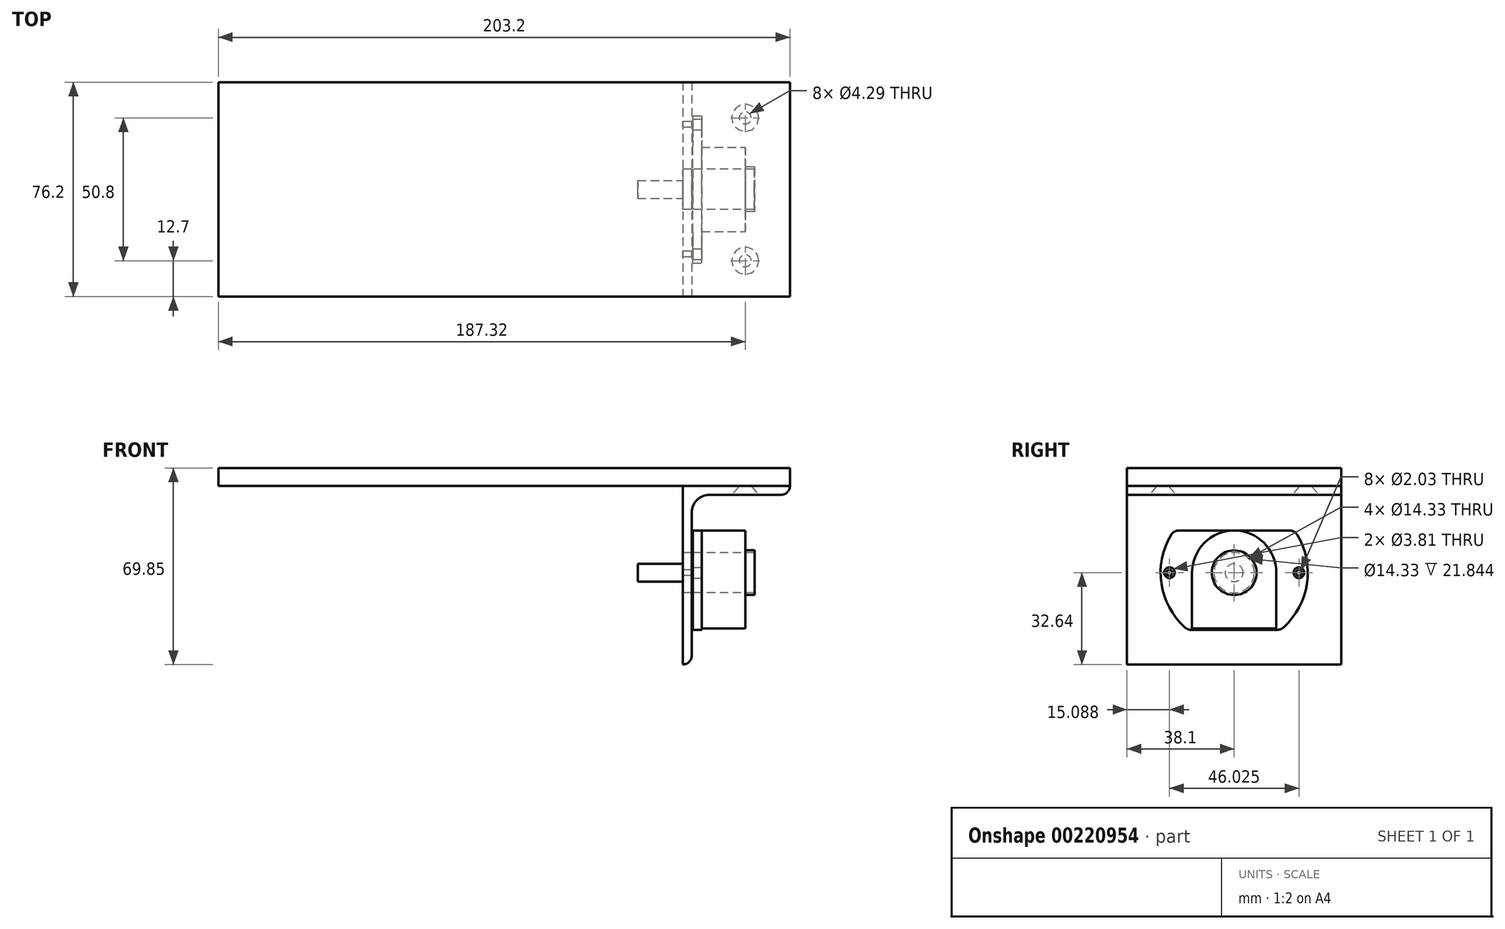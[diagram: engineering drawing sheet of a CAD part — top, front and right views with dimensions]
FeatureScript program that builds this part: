
annotation { "Feature Type Name" : "Feature", "Feature Type Description" : "" }
export const myFeature = defineFeature(function(context is Context, id is Id, definition is map)
    precondition{}
    {
        {
            var Q0;
            Q0=qCreatedBy(makeId("Right.planeOp"),FACE);
            var sketch = newSketch(context, id + "F0", { "sketchPlane" : qUnion([Q0])});
            skCircle(sketch, "E0", {"center": v(0, 0) * mm, "radius": 7.94 * mm});
            skCircle(sketch, "E1", {"center": v(0, 0) * mm, "radius": 14.99 * mm});
            skLineSegment(sketch, "E2", {"start": v(-14.99, 0) * mm, "end": v(-14.99, -19.81) * mm});
            skLineSegment(sketch, "E3", {"start": v(-14.99, -19.81) * mm, "end": v(14.99, -19.81) * mm});
            skLineSegment(sketch, "E4", {"start": v(14.99, -19.81) * mm, "end": v(14.99, 0) * mm});
            skSolve(sketch);
        }
        {
            var Q0;
            Q0=makeQuery(id+"F0.imprint","IMPRINT",FACE,{"disambiguationData":[TD([[makeQuery(id+"F0.imprint","IMPRINT",EDGE,{"derivedFrom":sQuery(id+"F0.wireOp",EDGE,"E0")}),1.0]])]});
            extrude(context, id + "F1", {"entities" : qUnion([Q0]), "depth" : 3.3 * mm});
        }
        {
            var Q0;
            Q0=makeQuery(id+"F0.imprint","IMPRINT",FACE,{"disambiguationData":[TD([[makeQuery(id+"F0.imprint","IMPRINT",EDGE,{"derivedFrom":sQuery(id+"F0.wireOp",EDGE,"E0")}),-1.0]])]});
            var Q1;
            {var subQ0=sQuery(id+"F0.wireOp",EDGE,"E2");Q1=makeQuery(id+"F0.imprint","IMPRINT",FACE,{"disambiguationData":[TD([[makeQuery(id+"F0.imprint","IMPRINT",EDGE,{"derivedFrom":subQ0}),1.0]])]});}
            var Q2;
            Q2=makeQuery(id+"F0.imprint","IMPRINT",FACE,{"disambiguationData":[TD([[makeQuery(id+"F0.imprint","IMPRINT",EDGE,{"derivedFrom":sQuery(id+"F0.wireOp",EDGE,"E0")}),1.0]])]});
            extrude(context, id + "F2", {"entities" : qUnion([Q0, Q1, Q2]), "operationType" : NewBodyOperationType.ADD, "oppositeDirection" : true, "depth" : 15.5 * mm});
        }
        {
            var Q0;
            Q0=makeQuery(id+"F2.opExtrude","CAP_FACE",FACE,{"disambiguationData":[OSD([sQuery(id+"F0.wireOp",EDGE,"E1"),sQuery(id+"F0.wireOp",EDGE,"E2"),sQuery(id+"F0.wireOp",EDGE,"E3"),sQuery(id+"F0.wireOp",EDGE,"E4")])],"isStart":false});
            var sketch = newSketch(context, id + "F3", { "sketchPlane" : qUnion([Q0])});
            skArc(sketch, "E5", {"start": v(-21.44, 14.99) * mm, "mid": v(-25.9, -3.64) * mm, "end": v(-16.48, -20.32) * mm});
            skLineSegment(sketch, "E6", {"start": v(21.44, 14.99) * mm, "end": v(-21.44, 14.99) * mm});
            skLineSegment(sketch, "E7", {"start": v(16.48, -20.32) * mm, "end": v(-16.48, -20.32) * mm});
            skArc(sketch, "E8.trimOffspring", {"start": v(16.48, -20.32) * mm, "mid": v(25.9, -3.64) * mm, "end": v(21.44, 14.99) * mm});
            skCircle(sketch, "E9", {"center": v(23.01, 0) * mm, "radius": 1.9 * mm});
            skCircle(sketch, "E10", {"center": v(-23.01, 0) * mm, "radius": 1.9 * mm});
            skLineSegment(sketch, "E11", {"start": v(23.01, 0) * mm, "end": v(-23.01, 0) * mm, "construction": true});
            skCircle(sketch, "E12", {"center": v(0, 0) * mm, "radius": 3.18 * mm});
            skSolve(sketch);
        }
        {
            var Q0;
            Q0=makeQuery(id+"F3.imprint","IMPRINT",FACE,{"disambiguationData":[TD([[makeQuery(id+"F3.imprint","IMPRINT",EDGE,{"derivedFrom":sQuery(id+"F3.wireOp",EDGE,"E12")}),-1.0]])]});
            var Q1;
            {var subQ2=sQuery(id+"F3.wireOp",EDGE,"E5");Q1=makeQuery(id+"F3.imprint","IMPRINT",FACE,{"disambiguationData":[TD([[makeQuery(id+"F3.imprint","IMPRINT",EDGE,{"derivedFrom":subQ2}),1.0]])]});}
            var Q2;
            Q2=makeQuery(id+"F3.imprint","IMPRINT",FACE,{"disambiguationData":[TD([[makeQuery(id+"F3.imprint","IMPRINT",EDGE,{"derivedFrom":sQuery(id+"F3.wireOp",EDGE,"E12")}),1.0]])]});
            extrude(context, id + "F4", {"entities" : qUnion([Q0, Q1, Q2]), "operationType" : NewBodyOperationType.ADD, "depth" : 3.17 * mm});
        }
        {
            var Q0;
            Q0=makeQuery(id+"F4.opExtrude","CAP_FACE",FACE,{"disambiguationData":[OSD([sQuery(id+"F3.wireOp",EDGE,"E5"),sQuery(id+"F3.wireOp",EDGE,"E6"),sQuery(id+"F3.wireOp",EDGE,"E7"),sQuery(id+"F3.wireOp",EDGE,"E8.trimOffspring"),sQuery(id+"F3.wireOp",EDGE,"E9"),sQuery(id+"F3.wireOp",EDGE,"E10")])],"isStart":false});
            var sketch = newSketch(context, id + "F5", { "sketchPlane" : qUnion([Q0])});
            skCircle(sketch, "E13", {"center": v(0, 0) * mm, "radius": 3.18 * mm});
            skCircle(sketch, "E14", {"center": v(0, 0) * mm, "radius": 6.35 * mm});
            skSolve(sketch);
        }
        {
            var Q0;
            Q0=makeQuery(id+"F5.imprint","IMPRINT",FACE,{"disambiguationData":[TD([[makeQuery(id+"F5.imprint","IMPRINT",EDGE,{"derivedFrom":sQuery(id+"F5.wireOp",EDGE,"E13")}),1.0]])]});
            extrude(context, id + "F6", {"entities" : qUnion([Q0]), "operationType" : NewBodyOperationType.ADD, "depth" : 19.56 * mm});
        }
        {
            var Q0;
            Q0=makeQuery(id+"F5.imprint","IMPRINT",FACE,{"disambiguationData":[TD([[makeQuery(id+"F5.imprint","IMPRINT",EDGE,{"derivedFrom":sQuery(id+"F5.wireOp",EDGE,"E13")}),-1.0]])]});
            extrude(context, id + "F7", {"entities" : qUnion([Q0]), "operationType" : NewBodyOperationType.ADD, "depth" : 0.5 * mm});
        }
        {
            var Q0;
            Q0=makeQuery(id+"F4.opExtrude","SWEPT_EDGE",EDGE,{"disambiguationData":[OSD([sQuery(id+"F3.wireOp",EDGE,"E6"),sQuery(id+"F3.wireOp",EDGE,"E8.trimOffspring")])]});
            var Q1;
            Q1=makeQuery(id+"F4.opExtrude","SWEPT_EDGE",EDGE,{"disambiguationData":[OSD([sQuery(id+"F3.wireOp",EDGE,"E5"),sQuery(id+"F3.wireOp",EDGE,"E6")])]});
            var Q2;
            Q2=makeQuery(id+"F4.opExtrude","SWEPT_EDGE",EDGE,{"disambiguationData":[OSD([sQuery(id+"F3.wireOp",EDGE,"E5"),sQuery(id+"F3.wireOp",EDGE,"E7")])]});
            var Q3;
            Q3=makeQuery(id+"F4.opExtrude","SWEPT_EDGE",EDGE,{"disambiguationData":[OSD([sQuery(id+"F3.wireOp",EDGE,"E7"),sQuery(id+"F3.wireOp",EDGE,"E8.trimOffspring")])]});
            fillet(context, id + "F8", {"entities" : qUnion([Q0, Q1, Q2, Q3]), "radius" : 3.17 * mm, "tangentPropagation" : true, "allowEdgeOverflow" : false});
        }
        {
            var Q0;
            Q0=qCreatedBy(makeId("Front.planeOp"),FACE);
            cPlane(context, id + "F9", {"entities" : qUnion([Q0]), "cplaneType" : CPlaneType.OFFSET, "offset" : 38.1 * mm, "width" : 152.4 * mm, "height" : 152.4 * mm});
        }
        {
            var Q0;
            Q0=qCreatedBy(id+"F9.planeOp",FACE);
            var sketch = newSketch(context, id + "F10", { "sketchPlane" : qUnion([Q0])});
            skLineSegment(sketch, "E15", {"start": v(-22.22, -32.64) * mm, "end": v(-22.23, 30.86) * mm});
            skLineSegment(sketch, "E16", {"start": v(-22.23, 30.86) * mm, "end": v(15.87, 30.86) * mm});
            skLineSegment(sketch, "E17", {"start": v(15.87, 30.86) * mm, "end": v(15.87, 27.69) * mm});
            skLineSegment(sketch, "E18", {"start": v(15.87, 27.69) * mm, "end": v(-19.05, 27.69) * mm});
            skLineSegment(sketch, "E19", {"start": v(-19.05, 27.69) * mm, "end": v(-19.05, -32.64) * mm});
            skLineSegment(sketch, "E20", {"start": v(-19.05, -32.64) * mm, "end": v(-22.22, -32.64) * mm});
            skSolve(sketch);
        }
        {
            var Q0;
            Q0 = qSketchRegion(id + "F10", true);
            extrude(context, id + "F11", {"entities" : qUnion([Q0]), "oppositeDirection" : true, "depth" : 76.2 * mm});
        }
        {
            var Q0;
            Q0=makeQuery(id+"F11.opExtrude","SWEPT_EDGE",EDGE,{"disambiguationData":[OSD([sQuery(id+"F10.wireOp",EDGE,"E17"),sQuery(id+"F10.wireOp",EDGE,"E18")])]});
            var Q1;
            Q1=makeQuery(id+"F11.opExtrude","SWEPT_EDGE",EDGE,{"disambiguationData":[OSD([sQuery(id+"F10.wireOp",EDGE,"E19"),sQuery(id+"F10.wireOp",EDGE,"E20")])]});
            fillet(context, id + "F12", {"entities" : qUnion([Q0, Q1]), "radius" : 3.17 * mm, "tangentPropagation" : true, "allowEdgeOverflow" : false});
        }
        {
            var Q0;
            Q0=makeQuery(id+"F11.opExtrude","SWEPT_EDGE",EDGE,{"disambiguationData":[OSD([sQuery(id+"F10.wireOp",EDGE,"E18"),sQuery(id+"F10.wireOp",EDGE,"E19")])]});
            fillet(context, id + "F13", {"entities" : qUnion([Q0]), "radius" : 6.35 * mm, "tangentPropagation" : true, "allowEdgeOverflow" : false});
        }
        {
            var Q0;
            Q0=makeQuery(id+"F11.opExtrude","SWEPT_FACE",FACE,{"disambiguationData":[OSD([sQuery(id+"F10.wireOp",EDGE,"E15")])]});
            var sketch = newSketch(context, id + "F14", { "sketchPlane" : qUnion([Q0])});
            skCircle(sketch, "E21.0", {"center": v(0, 0) * mm, "radius": 6.35 * mm, "construction": true});
            skCircle(sketch, "E22.0", {"center": v(0, 0) * mm, "radius": 7.16 * mm});
            skCircle(sketch, "E23.0", {"center": v(23.01, 0) * mm, "radius": 1.9 * mm, "construction": true});
            skCircle(sketch, "E23.1", {"center": v(-23.01, 0) * mm, "radius": 1.9 * mm, "construction": true});
            skCircle(sketch, "E24", {"center": v(23.01, 0) * mm, "radius": 1.02 * mm});
            skCircle(sketch, "E25", {"center": v(-23.01, 0) * mm, "radius": 1.02 * mm});
            skSolve(sketch);
        }
        {
            var Q0;
            Q0=makeQuery(id+"F14.imprint","IMPRINT",FACE,{"disambiguationData":[TD([[makeQuery(id+"F14.imprint","IMPRINT",EDGE,{"derivedFrom":sQuery(id+"F14.wireOp",EDGE,"E22.0")}),1.0]])]});
            var Q1;
            Q1=makeQuery(id+"F14.imprint","IMPRINT",FACE,{"disambiguationData":[TD([[makeQuery(id+"F14.imprint","IMPRINT",EDGE,{"derivedFrom":sQuery(id+"F14.wireOp",EDGE,"E24")}),1.0]])]});
            var Q2;
            Q2=makeQuery(id+"F14.imprint","IMPRINT",FACE,{"disambiguationData":[TD([[makeQuery(id+"F14.imprint","IMPRINT",EDGE,{"derivedFrom":sQuery(id+"F14.wireOp",EDGE,"E25")}),1.0]])]});
            var Q3;
            Q3=sQuery(id+"F14.wireOp",EDGE,"E21.0");
            var Q4;
            Q4=sQuery(id+"F14.wireOp",EDGE,"E22.0");
            extrude(context, id + "F15", {"entities" : qUnion([Q0, Q1, Q2]), "operationType" : NewBodyOperationType.REMOVE, "surfaceEntities" : qUnion([Q3, Q4]), "oppositeDirection" : true, "depth" : 25.4 * mm});
        }
        {
            var Q0;
            Q0=makeQuery(id+"F11.opExtrude","SWEPT_FACE",FACE,{"disambiguationData":[OSD([sQuery(id+"F10.wireOp",EDGE,"E16")])]});
            var sketch = newSketch(context, id + "F16", { "sketchPlane" : qUnion([Q0])});
            skLineSegment(sketch, "E26", {"start": v(-3.18, -38.1) * mm, "end": v(-3.18, 38.1) * mm, "construction": true});
            skCircle(sketch, "E27", {"center": v(-3.18, -29.4) * mm, "radius": 3.63 * mm});
            skCircle(sketch, "E28", {"center": v(-3.18, 28.84) * mm, "radius": 2.15 * mm});
            skSolve(sketch);
        }
        {
            var Q0;
            Q0=makeQuery(id+"F16.imprint","IMPRINT",FACE,{"disambiguationData":[TD([[makeQuery(id+"F16.imprint","IMPRINT",EDGE,{"derivedFrom":sQuery(id+"F16.wireOp",EDGE,"E27")}),-1.0]])]});
            var sketch = newSketch(context, id + "F17", { "sketchPlane" : qUnion([Q0])});
            skLineSegment(sketch, "E29.bottom", {"start": v(15.87, -38.1) * mm, "end": v(-187.33, -38.1) * mm});
            skLineSegment(sketch, "E29.top", {"start": v(15.87, 38.1) * mm, "end": v(-187.33, 38.1) * mm});
            skLineSegment(sketch, "E29.left", {"start": v(15.87, -38.1) * mm, "end": v(15.87, 38.1) * mm});
            skLineSegment(sketch, "E29.right", {"start": v(-187.33, -38.1) * mm, "end": v(-187.33, 38.1) * mm});
            skSolve(sketch);
        }
        {
            var Q0;
            Q0 = qSketchRegion(id + "F17", true);
            extrude(context, id + "F18", {"entities" : qUnion([Q0]), "depth" : 6.35 * mm});
        }
        {
            var Q0;
            Q0=makeQuery(id+"F11.opExtrude","SWEPT_FACE",FACE,{"disambiguationData":[OSD([sQuery(id+"F10.wireOp",EDGE,"E18")])]});
            var sketch = newSketch(context, id + "F19", { "sketchPlane" : qUnion([Q0])});
            skLineSegment(sketch, "E30", {"start": v(0, -38.1) * mm, "end": v(0, 38.1) * mm, "construction": true});
            skPoint(sketch, "E31", {"position": v(0, -25.4) * mm});
            skPoint(sketch, "E32", {"position": v(0, 25.4) * mm});
            skSolve(sketch);
        }
        {
            var Q0;
            Q0=sQuery(id+"F19.wireOp",VERTEX,"E31");
            var Q1;
            Q1=sQuery(id+"F19.wireOp",VERTEX,"E32");
            var Q2;
            Q2=makeQuery(id+"F11.opExtrude","SWEPT_BODY",BODY,{"disambiguationData":[OSD([sQuery(id+"F10.wireOp",EDGE,"E15"),sQuery(id+"F10.wireOp",EDGE,"E16"),sQuery(id+"F10.wireOp",EDGE,"E17"),sQuery(id+"F10.wireOp",EDGE,"E18"),sQuery(id+"F10.wireOp",EDGE,"E19"),sQuery(id+"F10.wireOp",EDGE,"E20")])]});
            hole(context, id + "F20", {"style" : HoleStyle.C_SINK, "endStyle" : HoleEndStyle.BLIND, "holeDiameter" : 4.3 * mm, "cSinkDiameter" : 9.52 * mm, "cSinkAngle" : 82 * degree, "holeDepth" : 19.05 * mm, "locations" : qUnion([Q0, Q1]), "scope" : qUnion([Q2])});
        }
    });
